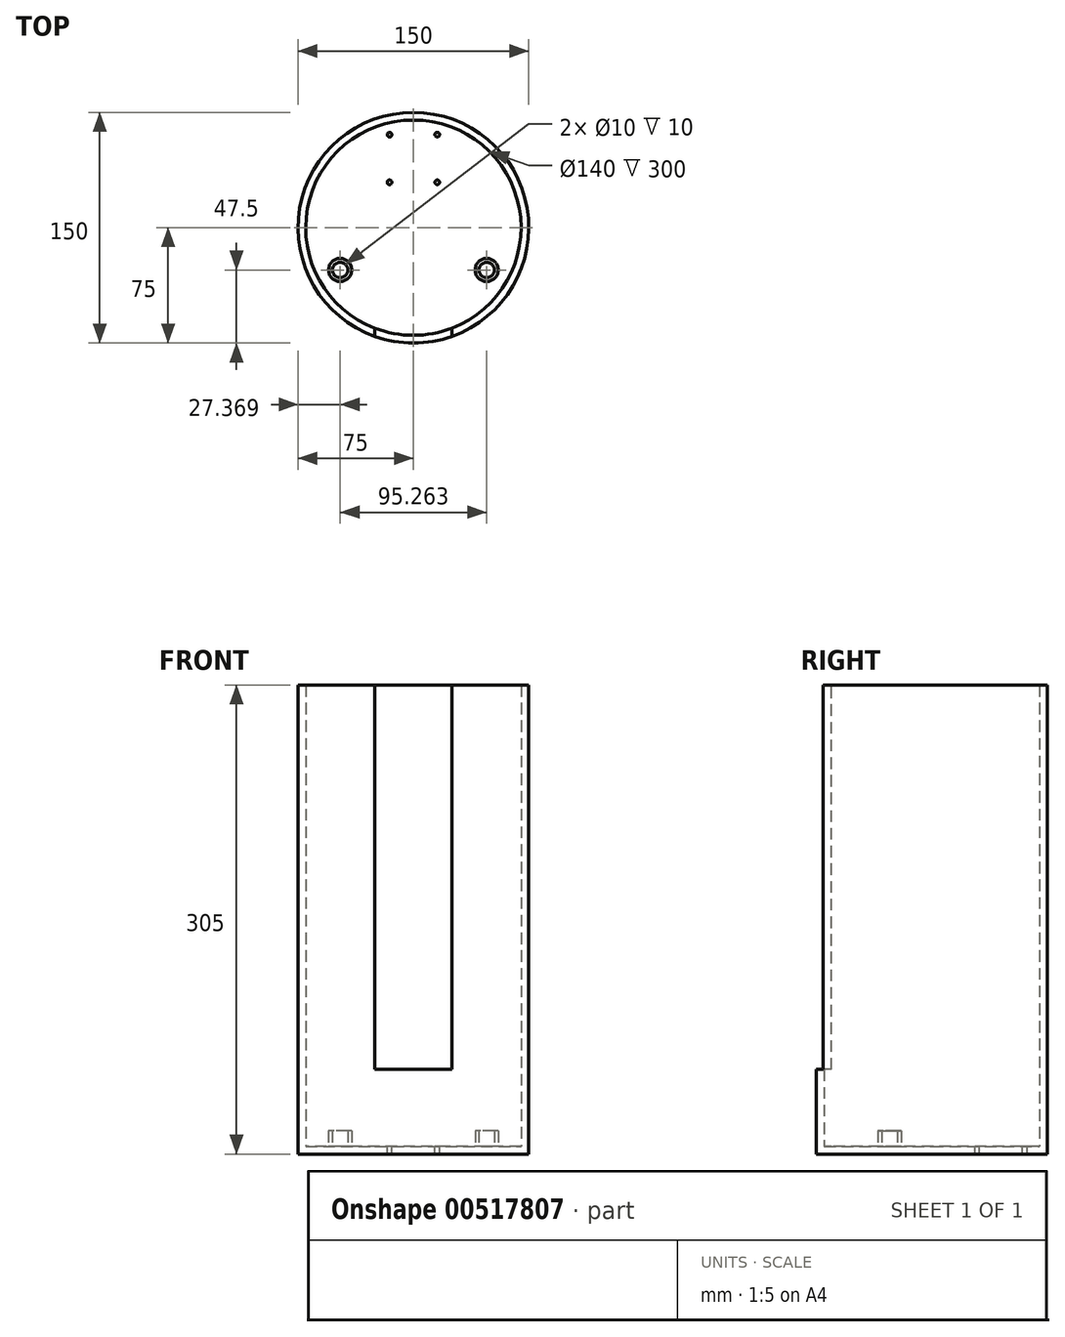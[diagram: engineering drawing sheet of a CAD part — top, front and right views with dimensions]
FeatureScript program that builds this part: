
annotation { "Feature Type Name" : "Feature", "Feature Type Description" : "" }
export const myFeature = defineFeature(function(context is Context, id is Id, definition is map)
    precondition{}
    {
        {
            var Q0;
            Q0=qCreatedBy(makeId("Top.planeOp"),FACE);
            var sketch = newSketch(context, id + "F0", { "sketchPlane" : qUnion([Q0])});
            skCircle(sketch, "E0", {"center": v(0, 0) * mm, "radius": 75 * mm});
            skSolve(sketch);
        }
        {
            var Q0;
            Q0 = qSketchRegion(id + "F0", true);
            extrude(context, id + "F1", {"entities" : qUnion([Q0]), "depth" : 5 * mm, "offsetDistance" : 25 * mm});
        }
        {
            var Q0;
            Q0=makeQuery(id+"F1.opExtrude","CAP_FACE",FACE,{"disambiguationData":[OSD([sQuery(id+"F0.wireOp",EDGE,"E0")])],"isStart":false});
            var sketch = newSketch(context, id + "F2", { "sketchPlane" : qUnion([Q0])});
            skCircle(sketch, "E1", {"center": v(0, 0) * mm, "radius": 75 * mm});
            skCircle(sketch, "E2", {"center": v(0, 0) * mm, "radius": 70 * mm});
            skSolve(sketch);
        }
        {
            var Q0;
            Q0=makeQuery(id+"F2.imprint","IMPRINT",FACE,{"disambiguationData":[TD([[makeQuery(id+"F2.imprint","IMPRINT",EDGE,{"derivedFrom":sQuery(id+"F2.wireOp",EDGE,"E1")}),1.0]])]});
            extrude(context, id + "F3", {"entities" : qUnion([Q0]), "operationType" : NewBodyOperationType.ADD, "depth" : 300 * mm, "offsetDistance" : 25 * mm});
        }
        {
            var Q0;
            Q0=makeQuery(id+"F3.opExtrude","CAP_FACE",FACE,{"disambiguationData":[OSD([sQuery(id+"F2.wireOp",EDGE,"E1"),sQuery(id+"F2.wireOp",EDGE,"E2")])],"isStart":false});
            var sketch = newSketch(context, id + "F4", { "sketchPlane" : qUnion([Q0])});
            skLineSegment(sketch, "E3.bottom", {"start": v(25, -39.96) * mm, "end": v(-25, -39.96) * mm});
            skLineSegment(sketch, "E3.top", {"start": v(25, -100.04) * mm, "end": v(-25, -100.04) * mm});
            skLineSegment(sketch, "E3.left", {"start": v(25, -39.96) * mm, "end": v(25, -100.04) * mm});
            skLineSegment(sketch, "E3.right", {"start": v(-25, -39.96) * mm, "end": v(-25, -100.04) * mm});
            skPoint(sketch, "E3.middle", {"position": v(0, -70) * mm});
            skSolve(sketch);
        }
        {
            var Q0;
            {var subQ0=sQuery(id+"F4.wireOp",EDGE,"E3.left");var subQ1=makeQuery(id+"F3.opExtrude","CAP_EDGE",EDGE,{"disambiguationData":[OSD([sQuery(id+"F2.wireOp",EDGE,"E1")])],"isStart":false});var subQ2=makeQuery(id+"F4.imprint","INTERSECT",VERTEX,{"derivedFrom":[subQ1,subQ0]});Q0=makeQuery(id+"F4.imprint","IMPRINT",FACE,{"disambiguationData":[TD([[makeQuery(id+"F4.imprint","IMPRINT",EDGE,{"disambiguationData":[TD([[subQ2,1.0]])],"derivedFrom":subQ0}),-1.0]])]});}
            extrude(context, id + "F5", {"entities" : qUnion([Q0]), "operationType" : NewBodyOperationType.REMOVE, "oppositeDirection" : true, "depth" : 250 * mm, "offsetDistance" : 25 * mm});
        }
        {
            var Q0;
            Q0=makeQuery(id+"F1.opExtrude","CAP_FACE",FACE,{"disambiguationData":[OSD([sQuery(id+"F0.wireOp",EDGE,"E0")])],"isStart":false});
            var sketch = newSketch(context, id + "F6", { "sketchPlane" : qUnion([Q0])});
            skLineSegment(sketch, "E4", {"start": v(0, 0) * mm, "end": v(0, 45) * mm});
            skLineSegment(sketch, "E5", {"start": v(0, 45) * mm, "end": v(0, 60.5) * mm});
            skLineSegment(sketch, "E6", {"start": v(0, 60.5) * mm, "end": v(15.5, 60.5) * mm});
            skLineSegment(sketch, "E7", {"start": v(0, 60.5) * mm, "end": v(-15.5, 60.5) * mm});
            skLineSegment(sketch, "E8", {"start": v(0, 0) * mm, "end": v(0, 29.5) * mm});
            skLineSegment(sketch, "E9", {"start": v(0, 29.5) * mm, "end": v(-15.5, 29.5) * mm});
            skLineSegment(sketch, "E10", {"start": v(0, 29.5) * mm, "end": v(15.5, 29.5) * mm});
            skCircle(sketch, "E11", {"center": v(-15.5, 60.5) * mm, "radius": 1.5 * mm});
            skCircle(sketch, "E12", {"center": v(15.5, 60.5) * mm, "radius": 1.5 * mm});
            skCircle(sketch, "E13", {"center": v(15.5, 29.5) * mm, "radius": 1.5 * mm});
            skCircle(sketch, "E14", {"center": v(-15.5, 29.5) * mm, "radius": 1.5 * mm});
            skSolve(sketch);
        }
        {
            var Q0;
            Q0=makeQuery(id+"F6.imprint","IMPRINT",FACE,{"disambiguationData":[TD([[makeQuery(id+"F6.imprint","IMPRINT",EDGE,{"derivedFrom":sQuery(id+"F6.wireOp",EDGE,"E11")}),1.0]])]});
            var Q1;
            Q1=makeQuery(id+"F6.imprint","IMPRINT",FACE,{"disambiguationData":[TD([[makeQuery(id+"F6.imprint","IMPRINT",EDGE,{"derivedFrom":sQuery(id+"F6.wireOp",EDGE,"E12")}),1.0]])]});
            var Q2;
            Q2=makeQuery(id+"F6.imprint","IMPRINT",FACE,{"disambiguationData":[TD([[makeQuery(id+"F6.imprint","IMPRINT",EDGE,{"derivedFrom":sQuery(id+"F6.wireOp",EDGE,"E13")}),1.0]])]});
            var Q3;
            Q3=makeQuery(id+"F6.imprint","IMPRINT",FACE,{"disambiguationData":[TD([[makeQuery(id+"F6.imprint","IMPRINT",EDGE,{"derivedFrom":sQuery(id+"F6.wireOp",EDGE,"E14")}),1.0]])]});
            extrude(context, id + "F7", {"entities" : qUnion([Q0, Q1, Q2, Q3]), "operationType" : NewBodyOperationType.REMOVE, "oppositeDirection" : true, "depth" : 25 * mm, "offsetDistance" : 25 * mm});
        }
        {
            var Q0;
            Q0=makeQuery(id+"F1.opExtrude","CAP_FACE",FACE,{"disambiguationData":[OSD([sQuery(id+"F0.wireOp",EDGE,"E0")])],"isStart":false});
            var sketch = newSketch(context, id + "F8", { "sketchPlane" : qUnion([Q0])});
            skLineSegment(sketch, "E15", {"start": v(0, 0) * mm, "end": v(0, 99.62) * mm});
            skLineSegment(sketch, "E16", {"start": v(0, 0) * mm, "end": v(47.63, -27.5) * mm});
            skLineSegment(sketch, "E17", {"start": v(0, 0) * mm, "end": v(-47.63, -27.5) * mm});
            skCircle(sketch, "E18", {"center": v(-47.63, -27.5) * mm, "radius": 7.5 * mm});
            skCircle(sketch, "E19", {"center": v(47.63, -27.5) * mm, "radius": 5 * mm});
            skCircle(sketch, "E20", {"center": v(47.63, -27.5) * mm, "radius": 7.5 * mm});
            skCircle(sketch, "E21", {"center": v(-47.63, -27.5) * mm, "radius": 5 * mm});
            skSolve(sketch);
        }
        {
            var Q0;
            Q0=makeQuery(id+"F8.imprint","IMPRINT",FACE,{"disambiguationData":[TD([[makeQuery(id+"F8.imprint","IMPRINT",EDGE,{"derivedFrom":sQuery(id+"F8.wireOp",EDGE,"E18")}),1.0]])]});
            var Q1;
            Q1=makeQuery(id+"F8.imprint","IMPRINT",FACE,{"disambiguationData":[TD([[makeQuery(id+"F8.imprint","IMPRINT",EDGE,{"derivedFrom":sQuery(id+"F8.wireOp",EDGE,"E19")}),-1.0]])]});
            extrude(context, id + "F9", {"entities" : qUnion([Q0, Q1]), "operationType" : NewBodyOperationType.ADD, "depth" : 10 * mm, "offsetDistance" : 25 * mm});
        }
    });
